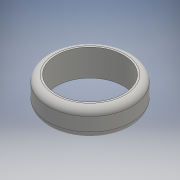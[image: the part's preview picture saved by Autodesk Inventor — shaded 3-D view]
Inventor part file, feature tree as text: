
AUTODESK INVENTOR PART (.ipt)
format: ipt  version: 2016 (Build 200138000, 138)  size: 130,048 bytes
history: native  units: mm
features: other x1, extrude x1, fillet x1, sketch x1
ambient origin geometry x8: Origin, YZ Plane, XZ Plane, XY Plane, X Axis, Y Axis, Z Axis, Center Point
bodies: Body1 (feature_tree)
feature tree (4):
  other  "ソリッド1"
  extrude  "押し出し1"  Depth=25.0mm
  fillet  "フィレット1"  Radius=20.0mm
  sketch  "スケッチ1"
